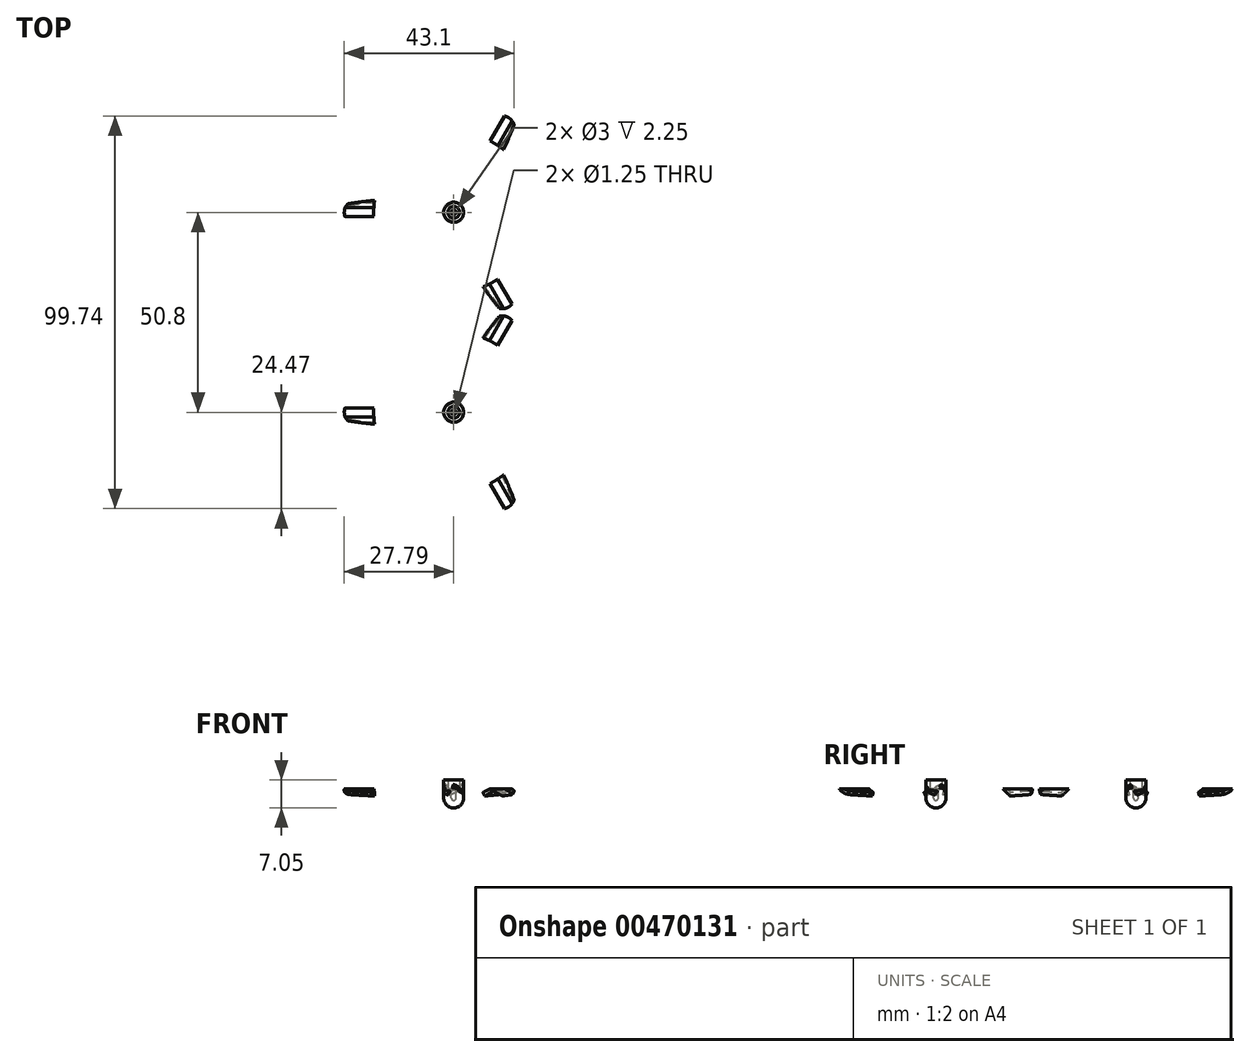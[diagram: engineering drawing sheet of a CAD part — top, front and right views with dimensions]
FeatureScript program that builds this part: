
annotation { "Feature Type Name" : "Feature", "Feature Type Description" : "" }
export const myFeature = defineFeature(function(context is Context, id is Id, definition is map)
    precondition{}
    {
        {
            var Q0;
            Q0=qCreatedBy(makeId("Top.planeOp"),FACE);
            var sketch = newSketch(context, id + "F0", { "sketchPlane" : qUnion([Q0])});
            skCircle(sketch, "E0", {"center": v(0, 0) * mm, "radius": 0.63 * mm});
            skCircle(sketch, "E1", {"center": v(0, 0) * mm, "radius": 1.5 * mm});
            skCircle(sketch, "E2.0", {"center": v(0, 0) * mm, "radius": 2.55 * mm});
            skArc(sketch, "E3", {"start": v(-1.98, 1.6) * mm, "mid": v(-14.75, 3.36) * mm, "end": v(-27.48, 1.31) * mm});
            skArc(sketch, "E4", {"start": v(-27.48, 1.31) * mm, "mid": v(-27.74, -0.54) * mm, "end": v(-26.84, -2.17) * mm});
            skArc(sketch, "E5", {"start": v(-26.84, -2.17) * mm, "mid": v(-13.84, -3.4) * mm, "end": v(-0.82, -2.42) * mm});
            skSolve(sketch);
        }
        {
            var Q0;
            Q0=makeQuery(id+"F0.imprint","IMPRINT",FACE,{"disambiguationData":[TD([[makeQuery(id+"F0.imprint","IMPRINT",EDGE,{"derivedFrom":sQuery(id+"F0.wireOp",EDGE,"E1")}),-1.0]])]});
            extrude(context, id + "F1", {"entities" : qUnion([Q0]), "endBound" : BoundingType.SYMMETRIC, "depth" : 4.5 * mm});
        }
        {
            var Q0;
            Q0=makeQuery(id+"F0.imprint","IMPRINT",FACE,{"disambiguationData":[TD([[makeQuery(id+"F0.imprint","IMPRINT",EDGE,{"derivedFrom":sQuery(id+"F0.wireOp",EDGE,"E0")}),-1.0]])]});
            extrude(context, id + "F2", {"entities" : qUnion([Q0]), "operationType" : NewBodyOperationType.ADD, "oppositeDirection" : true, "depth" : 2.25 * mm});
        }
        {
            var Q0;
            {var subQ0=sQuery(id+"F0.wireOp",EDGE,"E1");Q0=makeQuery(id+"F2.boolean.opBoolean","MERGE",FACE,{"derivedFrom":[makeQuery(id+"F1.opExtrude","CAP_FACE",FACE,{"disambiguationData":[OSD([subQ0,sQuery(id+"F0.wireOp",EDGE,"E2.0")])],"isStart":true}),makeQuery(id+"F2.opExtrude","CAP_FACE",FACE,{"disambiguationData":[OSD([sQuery(id+"F0.wireOp",EDGE,"E0"),subQ0])],"isStart":false})]});}
            var sketch = newSketch(context, id + "F3", { "sketchPlane" : qUnion([Q0])});
            skLineSegment(sketch, "E6", {"start": v(0, 2.55) * mm, "end": v(0, -2.55) * mm});
            skArc(sketch, "E7", {"start": v(0, -2.55) * mm, "mid": v(2.55, 0) * mm, "end": v(0, 2.55) * mm});
            skSolve(sketch);
        }
        {
            var Q0;
            {var subQ0=sQuery(id+"F3.wireOp",EDGE,"E7");Q0=makeQuery(id+"F3.imprint","IMPRINT",FACE,{"disambiguationData":[TD([[makeQuery(id+"F3.imprint","IMPRINT",EDGE,{"derivedFrom":subQ0}),-1.0]])]});}
            var Q1;
            Q1=sQuery(id+"F3.wireOp",EDGE,"E6");
            revolve(context, id + "F4", {"operationType" : NewBodyOperationType.ADD, "entities" : qUnion([Q0]), "axis" : qUnion([Q1]), "revolveType" : RevolveType.ONE_DIRECTION, "angle" : 180 * degree});
        }
        {
            var Q0;
            {var subQ0=sQuery(id+"F0.wireOp",EDGE,"E3");Q0=makeQuery(id+"F0.imprint","IMPRINT",FACE,{"disambiguationData":[TD([[makeQuery(id+"F0.imprint","IMPRINT",EDGE,{"derivedFrom":subQ0}),1.0]])]});}
            extrude(context, id + "F5", {"entities" : qUnion([Q0]), "endBound" : BoundingType.SYMMETRIC, "depth" : 1 * mm});
        }
        {
            var Q0;
            Q0=qCreatedBy(makeId("Top.planeOp"),FACE);
            var sketch = newSketch(context, id + "F6", { "sketchPlane" : qUnion([Q0])});
            skLineSegment(sketch, "E8", {"start": v(7.03, 0) * mm, "end": v(-6.93, 0) * mm});
            skSolve(sketch);
        }
        {
            var Q0;
            Q0=makeQuery(id+"F5.opExtrude","SWEPT_BODY",BODY,{"disambiguationData":[OSD([sQuery(id+"F0.wireOp",EDGE,"E2.0"),sQuery(id+"F0.wireOp",EDGE,"E3"),sQuery(id+"F0.wireOp",EDGE,"E4"),sQuery(id+"F0.wireOp",EDGE,"E5")])]});
            var Q1;
            Q1=sQuery(id+"F6.wireOp",EDGE,"E8");
            transform(context, id + "F7", {"entities" : qUnion([Q0]), "transformType" : TransformType.ROTATION, "transformAxis" : qUnion([Q1]), "angle" : 25 * degree, "oppositeDirection" : true, "makeCopy" : false});
        }
        {
            var Q0;
            Q0=makeQuery(id+"F5.opExtrude","SWEPT_BODY",BODY,{"disambiguationData":[OSD([sQuery(id+"F0.wireOp",EDGE,"E2.0"),sQuery(id+"F0.wireOp",EDGE,"E3"),sQuery(id+"F0.wireOp",EDGE,"E4"),sQuery(id+"F0.wireOp",EDGE,"E5")])]});
            var Q1;
            Q1=sQuery(id+"F0.wireOp",EDGE,"E0");
            circularPattern(context, id + "F8", {"entities" : qUnion([Q0]), "axis" : qUnion([Q1]), "angle" : 360 * degree, "instanceCount" : 3, "equalSpace" : true});
        }
        {
            var Q0;
            Q0=makeQuery(id+"F8.opPattern","COPY",BODY,{"derivedFrom":makeQuery(id+"F5.opExtrude","SWEPT_BODY",BODY,{"disambiguationData":[OSD([sQuery(id+"F0.wireOp",EDGE,"E2.0"),sQuery(id+"F0.wireOp",EDGE,"E3"),sQuery(id+"F0.wireOp",EDGE,"E4"),sQuery(id+"F0.wireOp",EDGE,"E5")])]}),"instanceName":"1"});
            var Q1;
            Q1=makeQuery(id+"F8.opPattern","COPY",BODY,{"derivedFrom":makeQuery(id+"F5.opExtrude","SWEPT_BODY",BODY,{"disambiguationData":[OSD([sQuery(id+"F0.wireOp",EDGE,"E2.0"),sQuery(id+"F0.wireOp",EDGE,"E3"),sQuery(id+"F0.wireOp",EDGE,"E4"),sQuery(id+"F0.wireOp",EDGE,"E5")])]}),"instanceName":"2"});
            var Q2;
            Q2=makeQuery(id+"F5.opExtrude","SWEPT_BODY",BODY,{"disambiguationData":[OSD([sQuery(id+"F0.wireOp",EDGE,"E2.0"),sQuery(id+"F0.wireOp",EDGE,"E3"),sQuery(id+"F0.wireOp",EDGE,"E4"),sQuery(id+"F0.wireOp",EDGE,"E5")])]});
            var Q3;
            Q3=makeQuery(id+"F1.opExtrude","SWEPT_BODY",BODY,{"disambiguationData":[OSD([sQuery(id+"F0.wireOp",EDGE,"E1"),sQuery(id+"F0.wireOp",EDGE,"E2.0")])]});
            var Q4;
            Q4=qCreatedBy(makeId("Front.planeOp"),FACE);
            transform(context, id + "F9", {"entities" : qUnion([Q0, Q1, Q2, Q3]), "transformType" : TransformType.TRANSLATION_DISTANCE, "transformDirection" : qUnion([Q4]), "distance" : 25.4 * mm, "makeCopy" : false});
        }
        {
            var Q0;
            Q0=makeQuery(id+"F1.opExtrude","CAP_FACE",FACE,{"disambiguationData":[OSD([sQuery(id+"F0.wireOp",EDGE,"E1"),sQuery(id+"F0.wireOp",EDGE,"E2.0")])],"isStart":false});
            var sketch = newSketch(context, id + "F10", { "sketchPlane" : qUnion([Q0])});
            skCircle(sketch, "E9", {"center": v(0, -25.4) * mm, "radius": 20.32 * mm});
            skCircle(sketch, "E10", {"center": v(0, -25.4) * mm, "radius": 40.7 * mm});
            skSolve(sketch);
        }
        {
            var Q0;
            Q0=makeQuery(id+"F10.imprint","IMPRINT",FACE,{"disambiguationData":[TD([[makeQuery(id+"F10.imprint","IMPRINT",EDGE,{"derivedFrom":sQuery(id+"F10.wireOp",EDGE,"E9")}),1.0]])]});
            extrude(context, id + "F11", {"entities" : qUnion([Q0]), "operationType" : NewBodyOperationType.REMOVE, "oppositeDirection" : true, "depth" : 4.47 * mm});
        }
        {
            var Q0;
            Q0=makeQuery(id+"F10.imprint","IMPRINT",FACE,{"disambiguationData":[TD([[makeQuery(id+"F10.imprint","IMPRINT",EDGE,{"derivedFrom":sQuery(id+"F10.wireOp",EDGE,"E10")}),1.0]])]});
            extrude(context, id + "F12", {"entities" : qUnion([Q0]), "operationType" : NewBodyOperationType.REMOVE, "oppositeDirection" : true, "depth" : 2.3 * mm});
        }
        {
            var Q0;
            Q0=makeQuery(id+"F10.imprint","IMPRINT",FACE,{"disambiguationData":[TD([[makeQuery(id+"F10.imprint","IMPRINT",EDGE,{"derivedFrom":sQuery(id+"F10.wireOp",EDGE,"E9")}),1.0]])]});
            extrude(context, id + "F13", {"entities" : qUnion([Q0]), "operationType" : NewBodyOperationType.REMOVE, "oppositeDirection" : true, "depth" : 4.6 * mm});
        }
        {
            var Q0;
            Q0=makeQuery(id+"F1.opExtrude","SWEPT_BODY",BODY,{"disambiguationData":[OSD([sQuery(id+"F0.wireOp",EDGE,"E1"),sQuery(id+"F0.wireOp",EDGE,"E2.0")])]});
            var Q1;
            Q1=makeQuery(id+"F5.opExtrude","SWEPT_BODY",BODY,{"disambiguationData":[OSD([sQuery(id+"F0.wireOp",EDGE,"E2.0"),sQuery(id+"F0.wireOp",EDGE,"E3"),sQuery(id+"F0.wireOp",EDGE,"E4"),sQuery(id+"F0.wireOp",EDGE,"E5")])]});
            var Q2;
            Q2=makeQuery(id+"F8.opPattern","COPY",BODY,{"derivedFrom":makeQuery(id+"F5.opExtrude","SWEPT_BODY",BODY,{"disambiguationData":[OSD([sQuery(id+"F0.wireOp",EDGE,"E2.0"),sQuery(id+"F0.wireOp",EDGE,"E3"),sQuery(id+"F0.wireOp",EDGE,"E4"),sQuery(id+"F0.wireOp",EDGE,"E5")])]}),"instanceName":"1"});
            var Q3;
            Q3=makeQuery(id+"F8.opPattern","COPY",BODY,{"derivedFrom":makeQuery(id+"F5.opExtrude","SWEPT_BODY",BODY,{"disambiguationData":[OSD([sQuery(id+"F0.wireOp",EDGE,"E2.0"),sQuery(id+"F0.wireOp",EDGE,"E3"),sQuery(id+"F0.wireOp",EDGE,"E4"),sQuery(id+"F0.wireOp",EDGE,"E5")])]}),"instanceName":"2"});
            var Q4;
            Q4=qCreatedBy(makeId("Front.planeOp"),FACE);
            mirror(context, id + "F14", {"entities" : qUnion([Q0, Q1, Q2, Q3]), "mirrorPlane" : qUnion([Q4])});
        }
    });
